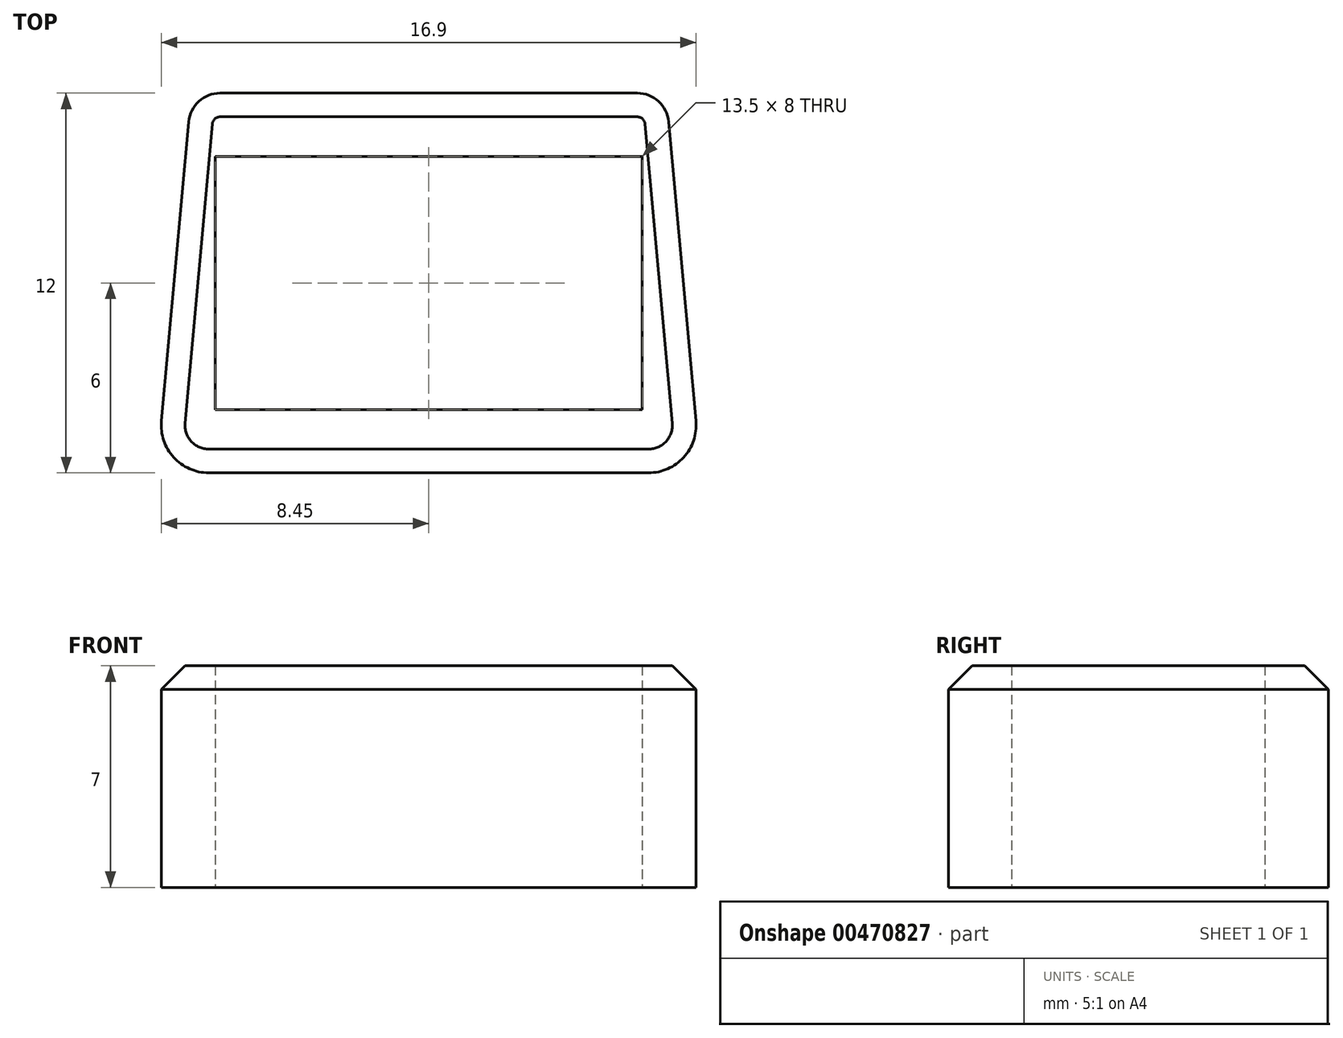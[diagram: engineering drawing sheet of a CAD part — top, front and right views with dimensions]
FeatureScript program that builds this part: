
annotation { "Feature Type Name" : "Feature", "Feature Type Description" : "" }
export const myFeature = defineFeature(function(context is Context, id is Id, definition is map)
    precondition{}
    {
        {
            var Q0;
            Q0=qCreatedBy(makeId("Top.planeOp"),FACE);
            var sketch = newSketch(context, id + "F0", { "sketchPlane" : qUnion([Q0])});
            skLineSegment(sketch, "E0.bottom", {"start": v(6.75, -4) * mm, "end": v(-6.75, -4) * mm});
            skLineSegment(sketch, "E0.top", {"start": v(6.75, 4) * mm, "end": v(-6.75, 4) * mm});
            skLineSegment(sketch, "E0.left", {"start": v(6.75, -4) * mm, "end": v(6.75, 4) * mm});
            skLineSegment(sketch, "E0.right", {"start": v(-6.75, -4) * mm, "end": v(-6.75, 4) * mm});
            skPoint(sketch, "E0.middle", {"position": v(0, 0) * mm});
            skLineSegment(sketch, "E1.bottom", {"start": v(6.95, -6) * mm, "end": v(-6.95, -6) * mm});
            skLineSegment(sketch, "E1.top", {"start": v(6.59, 6) * mm, "end": v(-6.59, 6) * mm});
            skPoint(sketch, "E2.visualSharp", {"position": v(-8.5, 6) * mm});
            skPoint(sketch, "E3.visualSharp", {"position": v(8.5, 6) * mm});
            skPoint(sketch, "E4.visualSharp", {"position": v(8.5, -6) * mm});
            skPoint(sketch, "E5.visualSharp", {"position": v(-8.5, -6) * mm});
            skArc(sketch, "E5.filletArc", {"start": v(-8.5, -5) * mm, "mid": v(-8.2, -5.7) * mm, "end": v(-7.5, -6) * mm});
            skLineSegment(sketch, "E6", {"start": v(-7.58, 5.1) * mm, "end": v(-8.44, -4.36) * mm});
            skLineSegment(sketch, "E7", {"start": v(7.58, 5.1) * mm, "end": v(8.44, -4.36) * mm});
            skPoint(sketch, "E8.visualSharp", {"position": v(-7.5, 6) * mm});
            skArc(sketch, "E8.filletArc", {"start": v(-6.59, 6) * mm, "mid": v(-7.26, 5.74) * mm, "end": v(-7.58, 5.1) * mm});
            skPoint(sketch, "E9.visualSharp", {"position": v(7.5, 6) * mm});
            skArc(sketch, "E9.filletArc", {"start": v(7.58, 5.1) * mm, "mid": v(7.26, 5.74) * mm, "end": v(6.59, 6) * mm});
            skArc(sketch, "E10.filletArc", {"start": v(6.95, -6) * mm, "mid": v(8.06, -5.51) * mm, "end": v(8.44, -4.36) * mm});
            skArc(sketch, "E11.filletArc", {"start": v(-8.44, -4.36) * mm, "mid": v(-8.06, -5.51) * mm, "end": v(-6.95, -6) * mm});
            skSolve(sketch);
        }
        {
            var Q0;
            Q0=makeQuery(id+"F0.imprint","IMPRINT",FACE,{"disambiguationData":[TD([[makeQuery(id+"F0.imprint","IMPRINT",EDGE,{"derivedFrom":sQuery(id+"F0.wireOp",EDGE,"E0.bottom")}),1.0]])]});
            extrude(context, id + "F1", {"entities" : qUnion([Q0]), "depth" : 7 * mm});
        }
        {
            var Q0;
            Q0=makeQuery(id+"F1.opExtrude","CAP_EDGE",EDGE,{"disambiguationData":[OSD([sQuery(id+"F0.wireOp",EDGE,"E1.top")])],"isStart":false});
            chamfer(context, id + "F2", {"entities" : qUnion([Q0]), "width" : .75 * mm, "tangentPropagation" : true});
        }
    });
